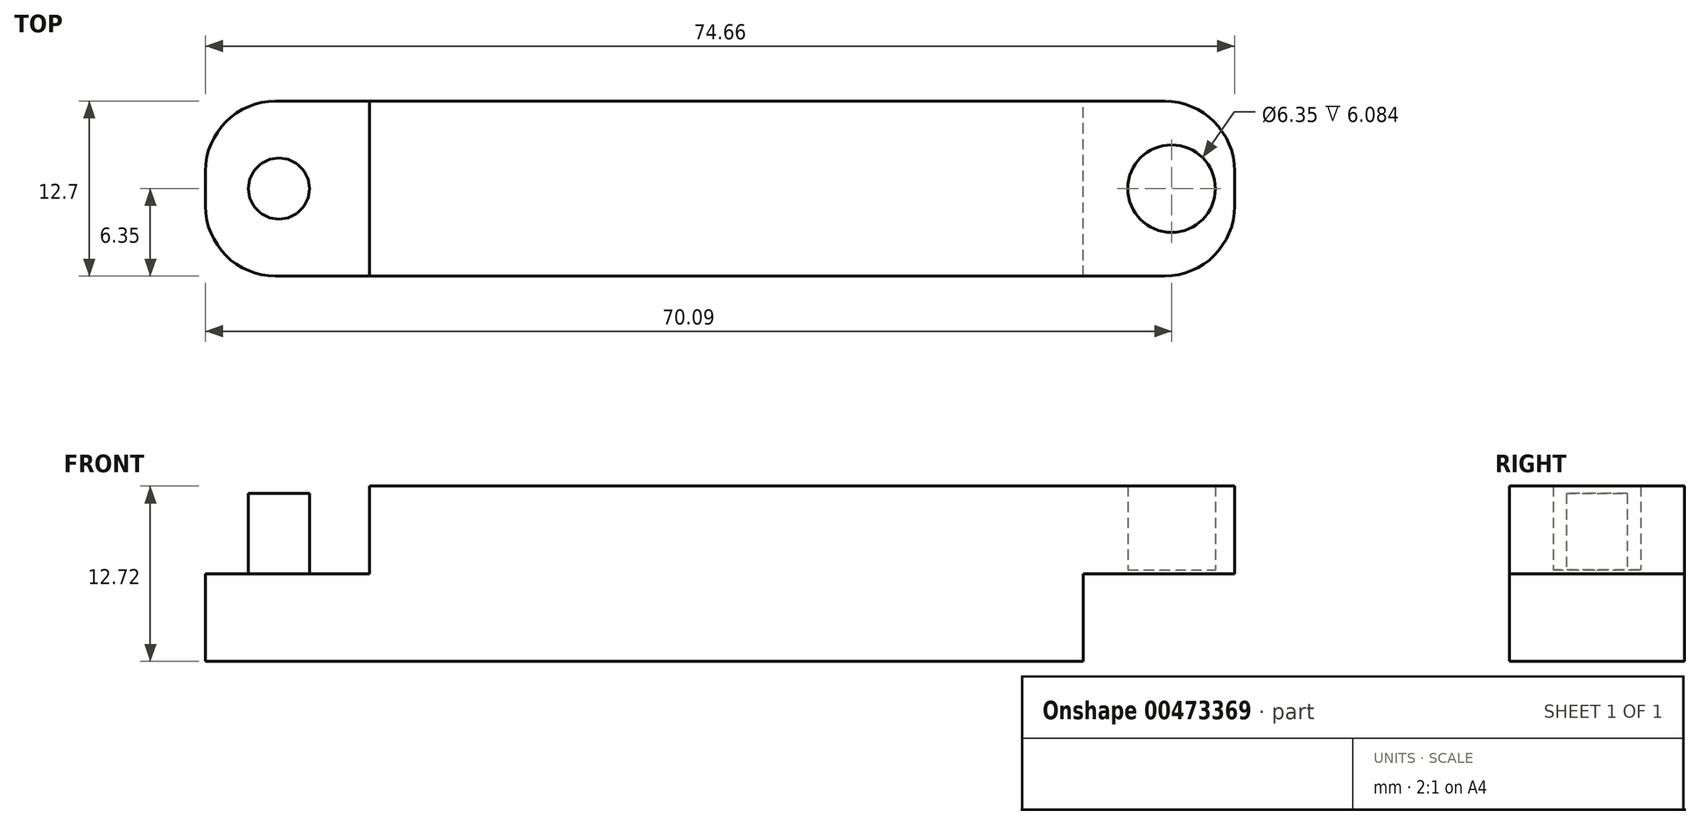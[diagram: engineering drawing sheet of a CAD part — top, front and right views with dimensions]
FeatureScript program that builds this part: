
annotation { "Feature Type Name" : "Feature", "Feature Type Description" : "" }
export const myFeature = defineFeature(function(context is Context, id is Id, definition is map)
    precondition{}
    {
        {
            var Q0;
            Q0=qCreatedBy(makeId("Front.planeOp"),FACE);
            var sketch = newSketch(context, id + "F0", { "sketchPlane" : qUnion([Q0])});
            skLineSegment(sketch, "E0.bottom", {"start": v(-29.31, 6.08) * mm, "end": v(22.5, 6.08) * mm});
            skLineSegment(sketch, "E0.top", {"start": v(-29.31, -6.64) * mm, "end": v(22.5, -6.64) * mm});
            skLineSegment(sketch, "E0.left", {"start": v(-29.31, 6.08) * mm, "end": v(-29.31, -6.64) * mm});
            skLineSegment(sketch, "E0.right", {"start": v(22.5, 6.08) * mm, "end": v(22.5, -6.64) * mm});
            skPoint(sketch, "E1.oppositeSnap0", {"position": v(-29.31, -0.28) * mm});
            skLineSegment(sketch, "E1.bottom", {"start": v(-29.31, -6.64) * mm, "end": v(-41.2, -6.64) * mm});
            skLineSegment(sketch, "E1.top", {"start": v(-29.31, -0.28) * mm, "end": v(-41.2, -0.28) * mm});
            skLineSegment(sketch, "E1.left", {"start": v(-29.31, -6.64) * mm, "end": v(-29.31, -0.28) * mm});
            skLineSegment(sketch, "E1.right", {"start": v(-41.2, -6.64) * mm, "end": v(-41.2, -0.28) * mm});
            skLineSegment(sketch, "E2.bottom", {"start": v(-37.52, -0.28) * mm, "end": v(-33.83, -0.28) * mm});
            skLineSegment(sketch, "E2.top", {"start": v(-37.52, 6.08) * mm, "end": v(-33.83, 6.08) * mm});
            skLineSegment(sketch, "E2.left", {"start": v(-37.52, -0.28) * mm, "end": v(-37.52, 6.08) * mm});
            skLineSegment(sketch, "E2.right", {"start": v(-33.83, -0.28) * mm, "end": v(-33.83, 6.08) * mm});
            skLineSegment(sketch, "E3.bottom", {"start": v(22.5, 6.08) * mm, "end": v(33.46, 6.08) * mm});
            skLineSegment(sketch, "E3.top", {"start": v(22.5, -0.28) * mm, "end": v(33.46, -0.28) * mm});
            skLineSegment(sketch, "E3.left", {"start": v(22.5, 6.08) * mm, "end": v(22.5, -0.28) * mm});
            skLineSegment(sketch, "E3.right", {"start": v(33.46, 6.08) * mm, "end": v(33.46, -0.28) * mm});
            skSolve(sketch);
        }
        {
            var Q0;
            Q0=makeQuery(id+"F0.imprint","IMPRINT",FACE,{"disambiguationData":[TD([[makeQuery(id+"F0.imprint","IMPRINT",EDGE,{"derivedFrom":sQuery(id+"F0.wireOp",EDGE,"E1.bottom")}),-1.0]])]});
            var Q1;
            Q1=makeQuery(id+"F0.imprint","IMPRINT",FACE,{"disambiguationData":[TD([[makeQuery(id+"F0.imprint","IMPRINT",EDGE,{"derivedFrom":sQuery(id+"F0.wireOp",EDGE,"E0.bottom")}),-1.0]])]});
            var Q2;
            Q2=makeQuery(id+"F0.imprint","IMPRINT",FACE,{"disambiguationData":[TD([[makeQuery(id+"F0.imprint","IMPRINT",EDGE,{"derivedFrom":sQuery(id+"F0.wireOp",EDGE,"E3.bottom")}),-1.0]])]});
            extrude(context, id + "F1", {"entities" : qUnion([Q0, Q1, Q2]), "depth" : 6.35 * mm, "offsetDistance" : 25.4 * mm});
        }
        {
            var Q0;
            Q0=makeQuery(id+"F1.opExtrude","CAP_FACE",FACE,{"disambiguationData":[OSD([sQuery(id+"F0.wireOp",EDGE,"E0.bottom"),sQuery(id+"F0.wireOp",EDGE,"E0.top"),sQuery(id+"F0.wireOp",EDGE,"E0.left"),sQuery(id+"F0.wireOp",EDGE,"E0.right"),sQuery(id+"F0.wireOp",EDGE,"E1.bottom"),sQuery(id+"F0.wireOp",EDGE,"E1.top"),sQuery(id+"F0.wireOp",EDGE,"E1.right"),sQuery(id+"F0.wireOp",EDGE,"E2.bottom"),sQuery(id+"F0.wireOp",EDGE,"E3.bottom"),sQuery(id+"F0.wireOp",EDGE,"E3.top"),sQuery(id+"F0.wireOp",EDGE,"E3.right")])],"isStart":true});
            extrude(context, id + "F2", {"entities" : qUnion([Q0]), "operationType" : NewBodyOperationType.ADD, "depth" : 6.35 * mm});
        }
        {
            var Q0;
            Q0=makeQuery(id+"F1.opExtrude","CAP_EDGE",EDGE,{"disambiguationData":[OSD([sQuery(id+"F0.wireOp",EDGE,"E1.right")])],"isStart":false});
            var Q1;
            Q1=makeQuery(id+"F2.opExtrude","CAP_EDGE",EDGE,{"disambiguationData":[OSD([sQuery(id+"F0.wireOp",EDGE,"E1.right")])],"isStart":false});
            var Q2;
            Q2=makeQuery(id+"F1.opExtrude","CAP_EDGE",EDGE,{"disambiguationData":[OSD([sQuery(id+"F0.wireOp",EDGE,"E3.right")])],"isStart":false});
            var Q3;
            Q3=makeQuery(id+"F2.opExtrude","CAP_EDGE",EDGE,{"disambiguationData":[OSD([sQuery(id+"F0.wireOp",EDGE,"E3.right")])],"isStart":false});
            fillet(context, id + "F3", {"entities" : qUnion([Q0, Q1, Q2, Q3]), "radius" : 5.08 * mm, "tangentPropagation" : true, "allowEdgeOverflow" : false});
        }
        {
            var Q0;
            Q0=qCreatedBy(makeId("Top.planeOp"),FACE);
            var sketch = newSketch(context, id + "F4", { "sketchPlane" : qUnion([Q0])});
            skPoint(sketch, "E4", {"position": v(28.9, 0) * mm});
            skCircle(sketch, "E5", {"center": v(28.9, 0) * mm, "radius": 3.18 * mm});
            skSolve(sketch);
        }
        {
            var Q0;
            Q0=sQuery(id+"F4.wireOp",VERTEX,"E4");
            var Q1;
            Q1=makeQuery(id+"F1.opExtrude","SWEPT_BODY",BODY,{"disambiguationData":[OSD([sQuery(id+"F0.wireOp",EDGE,"E0.bottom"),sQuery(id+"F0.wireOp",EDGE,"E0.top"),sQuery(id+"F0.wireOp",EDGE,"E0.left"),sQuery(id+"F0.wireOp",EDGE,"E0.right"),sQuery(id+"F0.wireOp",EDGE,"E1.bottom"),sQuery(id+"F0.wireOp",EDGE,"E1.top"),sQuery(id+"F0.wireOp",EDGE,"E1.right"),sQuery(id+"F0.wireOp",EDGE,"E2.bottom"),sQuery(id+"F0.wireOp",EDGE,"E3.bottom"),sQuery(id+"F0.wireOp",EDGE,"E3.top"),sQuery(id+"F0.wireOp",EDGE,"E3.right")])]});
            hole(context, id + "F5", {"style" : HoleStyle.SIMPLE, "endStyle" : HoleEndStyle.THROUGH, "oppositeDirection" : true, "holeDiameter" : 6.35 * mm, "isTappedThrough" : true, "tappedDepth" : 12.7 * mm, "tapClearance" : 3, "locations" : qUnion([Q0]), "scope" : qUnion([Q1]), "majorDiameter" : 6.35 * mm});
        }
        {
            var Q0;
            {var subQ0=sQuery(id+"F0.wireOp",EDGE,"E1.bottom");var subQ1=sQuery(id+"F0.wireOp",EDGE,"E0.top");Q0=makeQuery(id+"F2.boolean.opBoolean","MERGE",FACE,{"derivedFrom":[makeQuery(id+"F1.opExtrude","SWEPT_FACE",FACE,{"disambiguationData":[OSD([subQ1,subQ0])]}),makeQuery(id+"F2.opExtrude","SWEPT_FACE",FACE,{"disambiguationData":[OSD([subQ1,subQ0])]})]});}
            var sketch = newSketch(context, id + "F6", { "sketchPlane" : qUnion([Q0])});
            skCircle(sketch, "E6", {"center": v(-35.88, 0) * mm, "radius": 2.22 * mm});
            skSolve(sketch);
        }
        {
            var Q0;
            Q0=makeQuery(id+"F6.imprint","IMPRINT",FACE,{"disambiguationData":[TD([[makeQuery(id+"F6.imprint","IMPRINT",EDGE,{"derivedFrom":sQuery(id+"F6.wireOp",EDGE,"E6")}),1.0]])]});
            var Q1;
            Q1=sQuery(id+"F6.wireOp",EDGE,"E6");
            extrude(context, id + "F7", {"entities" : qUnion([Q0]), "operationType" : NewBodyOperationType.ADD, "surfaceEntities" : qUnion([Q1]), "oppositeDirection" : true, "depth" : 12.2 * mm, "offsetDistance" : 25.4 * mm});
        }
    });
